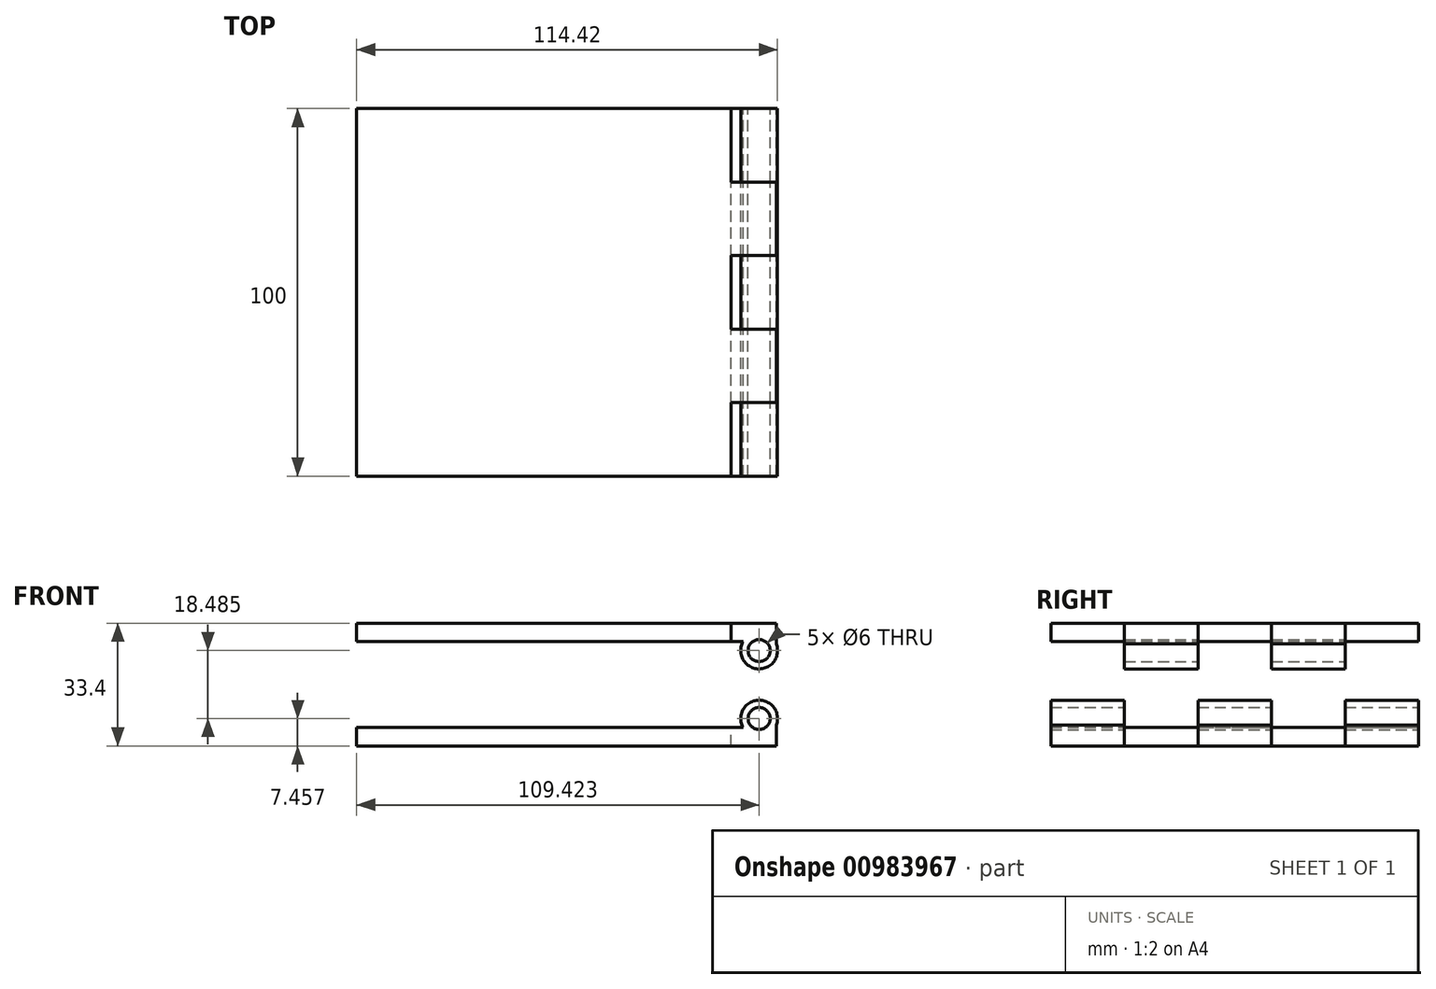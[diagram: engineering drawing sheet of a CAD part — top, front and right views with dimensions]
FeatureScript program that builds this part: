
annotation { "Feature Type Name" : "Feature", "Feature Type Description" : "" }
export const myFeature = defineFeature(function(context is Context, id is Id, definition is map)
    precondition{}
    {
        {
            var Q0;
            Q0=qCreatedBy(makeId("Front.planeOp"),FACE);
            var sketch = newSketch(context, id + "F0", { "sketchPlane" : qUnion([Q0])});
            skLineSegment(sketch, "E0.bottom", {"start": v(48.03, 2.5) * mm, "end": v(-57.04, 2.5) * mm});
            skLineSegment(sketch, "E0.top", {"start": v(57.04, -2.5) * mm, "end": v(-57.04, -2.5) * mm});
            skLineSegment(sketch, "E0.left", {"start": v(57.04, 3.14) * mm, "end": v(57.04, -2.5) * mm});
            skLineSegment(sketch, "E0.right", {"start": v(-57.04, 2.5) * mm, "end": v(-57.04, -2.5) * mm});
            skPoint(sketch, "E0.middle", {"position": v(0, 0) * mm});
            skArc(sketch, "E1", {"start": v(57.04, 3.14) * mm, "mid": v(52.03, 9.94) * mm, "end": v(48.03, 2.5) * mm});
            skPoint(sketch, "E1.first.point", {"position": v(51.73, 0) * mm});
            skPoint(sketch, "E1.first.point.positionSnap0", {"position": v(57.04, 0) * mm});
            skPoint(sketch, "E1.second.point", {"position": v(53.34, 9.87) * mm});
            skPoint(sketch, "E1.third.point", {"position": v(48.03, 2.5) * mm});
            skPoint(sketch, "E2.orphan", {"position": v(57.04, 2.5) * mm});
            skCircle(sketch, "E3", {"center": v(52.38, 4.96) * mm, "radius": 3 * mm});
            skSolve(sketch);
        }
        {
            var Q0;
            Q0=makeQuery(id+"F0.imprint","IMPRINT",FACE,{"disambiguationData":[TD([[makeQuery(id+"F0.imprint","IMPRINT",EDGE,{"derivedFrom":sQuery(id+"F0.wireOp",EDGE,"E0.bottom")}),1.0]])]});
            extrude(context, id + "F1", {"entities" : qUnion([Q0]), "depth" : 50 * mm, "offsetDistance" : 25 * mm, "hasSecondDirection" : true, "secondDirectionOppositeDirection" : true, "secondDirectionDepth" : 50 * mm});
        }
        {
            var Q0;
            Q0=qCreatedBy(makeId("Top.planeOp"),FACE);
            cPlane(context, id + "F2", {"entities" : qUnion([Q0]), "cplaneType" : CPlaneType.OFFSET, "offset" : 13.1 * mm, "width" : 150 * mm, "height" : 150 * mm});
        }
        {
            var Q0;
            Q0=qCreatedBy(id+"F2.planeOp",FACE);
            var sketch = newSketch(context, id + "F3", { "sketchPlane" : qUnion([Q0])});
            skLineSegment(sketch, "E4.bottom", {"start": v(44.73, 50) * mm, "end": v(66.75, 50) * mm});
            skLineSegment(sketch, "E4.left", {"start": v(44.73, 50) * mm, "end": v(44.73, -50) * mm});
            skLineSegment(sketch, "E4.right", {"start": v(66.75, 50) * mm, "end": v(66.75, -50) * mm});
            skLineSegment(sketch, "E5", {"start": v(44.73, 30) * mm, "end": v(66.75, 30) * mm});
            skLineSegment(sketch, "E6", {"start": v(44.73, 10) * mm, "end": v(66.75, 10) * mm});
            skLineSegment(sketch, "E7", {"start": v(44.73, -10) * mm, "end": v(66.75, -10) * mm});
            skLineSegment(sketch, "E8", {"start": v(44.73, -30) * mm, "end": v(66.75, -30) * mm});
            skLineSegment(sketch, "E9", {"start": v(44.73, -50) * mm, "end": v(69.98, -50) * mm});
            skSolve(sketch);
        }
        {
            var Q0;
            Q0=qCreatedBy(makeId("Top.planeOp"),FACE);
            cPlane(context, id + "F4", {"entities" : qUnion([Q0]), "cplaneType" : CPlaneType.OFFSET, "offset" : 14.2 * mm, "width" : 150 * mm, "height" : 150 * mm});
        }
        {
            var Q0;
            Q0=makeQuery(id+"F1.opExtrude","SWEPT_BODY",BODY,{"disambiguationData":[OSD([sQuery(id+"F0.wireOp",EDGE,"E0.bottom"),sQuery(id+"F0.wireOp",EDGE,"E0.top"),sQuery(id+"F0.wireOp",EDGE,"E0.left"),sQuery(id+"F0.wireOp",EDGE,"E0.right"),sQuery(id+"F0.wireOp",EDGE,"E1"),sQuery(id+"F0.wireOp",EDGE,"E3")])]});
            var Q1;
            Q1=qCreatedBy(id+"F4.planeOp",FACE);
            mirror(context, id + "F5", {"entities" : qUnion([Q0]), "mirrorPlane" : qUnion([Q1])});
        }
        {
            var Q0;
            {var subQ0=sQuery(id+"F3.wireOp",EDGE,"E5");Q0=makeQuery(id+"F3.imprint","IMPRINT",FACE,{"disambiguationData":[TD([[makeQuery(id+"F3.imprint","IMPRINT",EDGE,{"derivedFrom":subQ0}),-1.0]])]});}
            var Q1;
            {var subQ0=sQuery(id+"F3.wireOp",EDGE,"E7");Q1=makeQuery(id+"F3.imprint","IMPRINT",FACE,{"disambiguationData":[TD([[makeQuery(id+"F3.imprint","IMPRINT",EDGE,{"derivedFrom":subQ0}),-1.0]])]});}
            extrude(context, id + "F6", {"entities" : qUnion([Q0, Q1]), "operationType" : NewBodyOperationType.REMOVE, "oppositeDirection" : true, "depth" : 25 * mm, "offsetDistance" : 25 * mm});
        }
        {
            var Q0;
            {var subQ0=sQuery(id+"F3.wireOp",EDGE,"E4.bottom");Q0=makeQuery(id+"F3.imprint","IMPRINT",FACE,{"disambiguationData":[TD([[makeQuery(id+"F3.imprint","IMPRINT",EDGE,{"derivedFrom":subQ0}),-1.0]])]});}
            var Q1;
            {var subQ0=sQuery(id+"F3.wireOp",EDGE,"E6");Q1=makeQuery(id+"F3.imprint","IMPRINT",FACE,{"disambiguationData":[TD([[makeQuery(id+"F3.imprint","IMPRINT",EDGE,{"derivedFrom":subQ0}),-1.0]])]});}
            var Q2;
            {var subQ3=sQuery(id+"F3.wireOp",EDGE,"E8");Q2=makeQuery(id+"F3.imprint","IMPRINT",FACE,{"disambiguationData":[TD([[makeQuery(id+"F3.imprint","IMPRINT",EDGE,{"derivedFrom":subQ3}),-1.0]])]});}
            extrude(context, id + "F7", {"entities" : qUnion([Q0, Q1, Q2]), "operationType" : NewBodyOperationType.REMOVE, "depth" : 25 * mm, "offsetDistance" : 25 * mm});
        }
    });
